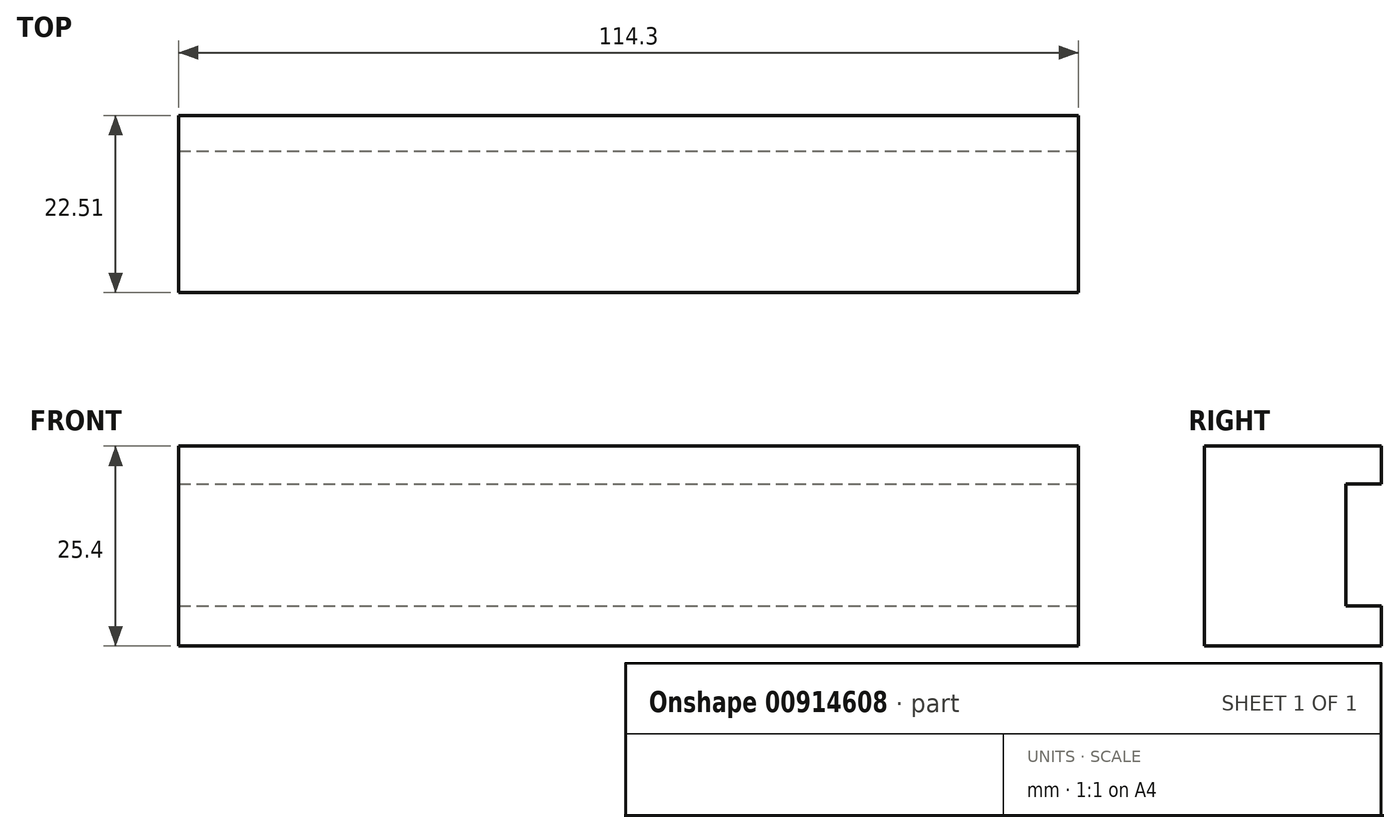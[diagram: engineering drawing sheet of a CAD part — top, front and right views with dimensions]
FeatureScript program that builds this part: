
annotation { "Feature Type Name" : "Feature", "Feature Type Description" : "" }
export const myFeature = defineFeature(function(context is Context, id is Id, definition is map)
    precondition{}
    {
        {
            var Q0;
            Q0=qCreatedBy(makeId("Top.planeOp"),FACE);
            var sketch = newSketch(context, id + "F0", { "sketchPlane" : qUnion([Q0])});
            skLineSegment(sketch, "E0.bottom", {"start": v(-51.58, -20.81) * mm, "end": v(62.72, -20.81) * mm});
            skLineSegment(sketch, "E0.top", {"start": v(-51.58, -43.32) * mm, "end": v(62.72, -43.32) * mm});
            skLineSegment(sketch, "E0.left", {"start": v(-51.58, -20.81) * mm, "end": v(-51.58, -43.32) * mm});
            skLineSegment(sketch, "E0.right", {"start": v(62.72, -20.81) * mm, "end": v(62.72, -43.32) * mm});
            skLineSegment(sketch, "E1.bottom", {"start": v(-51.58, -25.33) * mm, "end": v(62.72, -25.33) * mm});
            skLineSegment(sketch, "E1.left", {"start": v(-51.58, -25.33) * mm, "end": v(-51.58, -43.32) * mm});
            skLineSegment(sketch, "E1.right", {"start": v(62.72, -25.33) * mm, "end": v(62.72, -43.32) * mm});
            skSolve(sketch);
        }
        {
            var Q0;
            Q0 = qSketchRegion(id + "F0", true);
            extrude(context, id + "F1", {"entities" : qUnion([Q0]), "oppositeDirection" : true, "depth" : 5.08 * mm, "offsetDistance" : 25.4 * mm});
        }
        {
            var Q0;
            Q0=makeQuery(id+"F0.imprint","IMPRINT",FACE,{"disambiguationData":[TD([[makeQuery(id+"F0.imprint","IMPRINT",EDGE,{"derivedFrom":sQuery(id+"F0.wireOp",EDGE,"E1.bottom")}),-1.0]])]});
            extrude(context, id + "F2", {"entities" : qUnion([Q0]), "operationType" : NewBodyOperationType.ADD, "depth" : 15.5 * mm, "offsetDistance" : 25.4 * mm});
        }
        {
            var Q0;
            Q0 = qSketchRegion(id + "F0", true);
            extrude(context, id + "F3", {"entities" : qUnion([Q0]), "operationType" : NewBodyOperationType.ADD, "depth" : 20.32 * mm, "offsetDistance" : 25.4 * mm, "hasSecondDirection" : true, "secondDirectionOppositeDirection" : false, "secondDirectionDepth" : 15.5 * mm});
        }
    });
